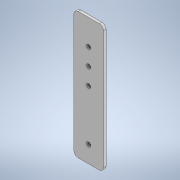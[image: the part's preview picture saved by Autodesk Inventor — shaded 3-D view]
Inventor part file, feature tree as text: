
AUTODESK INVENTOR PART (.ipt)
format: ipt  version: 2021 (Build 250183000, 183)  size: 107,008 bytes
history: native  units: mm
features: other x1, extrude x1, sketch x1
ambient origin geometry x8: Origin, YZ Plane, XZ Plane, XY Plane, X Axis, Y Axis, Z Axis, Center Point
bodies: Body1 (feature_tree)
feature tree (3):
  other  "Sólido1"
  extrude  "Extrusión1"  [1 undecoded]
  sketch  "Boceto1"  dims[d13=3.0mm d14=0.0mm]
note: 1 required parameter value undecoded (feature->parameter linkage not recoverable at this tier; creation-order binding heuristic only, values carry confidence <= 0.55)
